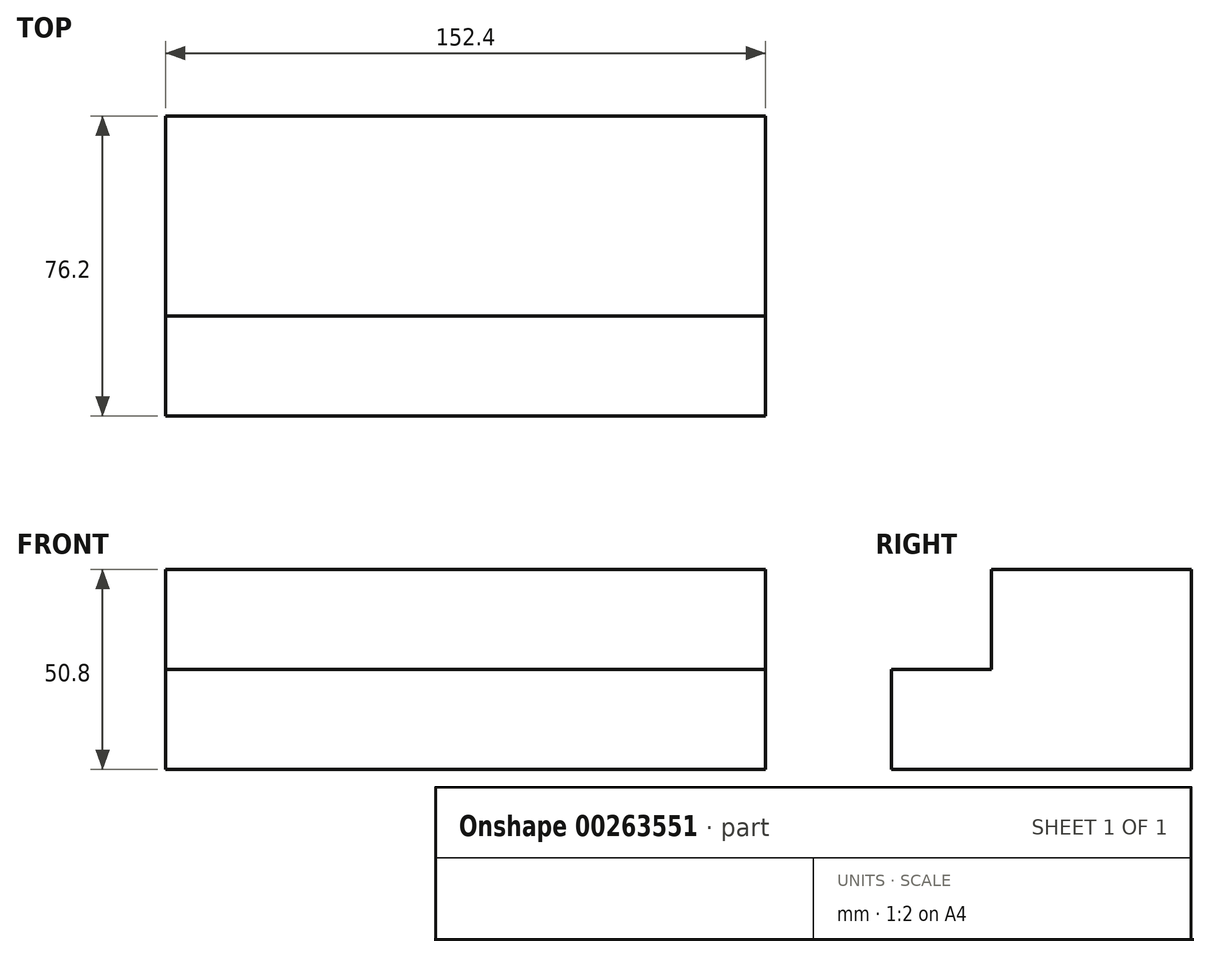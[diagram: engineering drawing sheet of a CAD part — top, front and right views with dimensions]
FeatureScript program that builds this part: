
annotation { "Feature Type Name" : "Feature", "Feature Type Description" : "" }
export const myFeature = defineFeature(function(context is Context, id is Id, definition is map)
    precondition{}
    {
        {
            var Q0;
            Q0=qCreatedBy(makeId("Front.planeOp"),FACE);
            var sketch = newSketch(context, id + "F0", { "sketchPlane" : qUnion([Q0])});
            skLineSegment(sketch, "E0", {"start": v(-61.88, -38.85) * mm, "end": v(90.52, -38.85) * mm});
            skLineSegment(sketch, "E1", {"start": v(-61.88, -38.85) * mm, "end": v(-61.88, -13.45) * mm});
            skLineSegment(sketch, "E2", {"start": v(-61.88, -13.45) * mm, "end": v(-61.88, 11.95) * mm});
            skLineSegment(sketch, "E3", {"start": v(90.52, -38.85) * mm, "end": v(90.52, -13.45) * mm});
            skLineSegment(sketch, "E4", {"start": v(90.52, -13.45) * mm, "end": v(90.52, 11.95) * mm});
            skLineSegment(sketch, "E5", {"start": v(90.52, 11.95) * mm, "end": v(-61.88, 11.95) * mm});
            skSolve(sketch);
        }
        {
            var Q0;
            Q0=makeQuery(id+"F0.imprint","IMPRINT",FACE,{"disambiguationData":[TD([[makeQuery(id+"F0.imprint","IMPRINT",EDGE,{"derivedFrom":sQuery(id+"F0.wireOp",EDGE,"E0")}),1.0]])]});
            extrude(context, id + "F1", {"entities" : qUnion([Q0]), "depth" : 76.2 * mm});
        }
        {
            var Q0;
            Q0=makeQuery(id+"F1.opExtrude","SWEPT_FACE",FACE,{"disambiguationData":[OSD([sQuery(id+"F0.wireOp",EDGE,"E3"),sQuery(id+"F0.wireOp",EDGE,"E4")])]});
            var sketch = newSketch(context, id + "F2", { "sketchPlane" : qUnion([Q0])});
            skLineSegment(sketch, "E6", {"start": v(-76.2, -38.85) * mm, "end": v(-76.2, -13.45) * mm});
            skLineSegment(sketch, "E7", {"start": v(-76.2, -13.45) * mm, "end": v(-50.8, -13.45) * mm});
            skLineSegment(sketch, "E8", {"start": v(-50.8, -13.45) * mm, "end": v(-50.8, 11.95) * mm});
            skSolve(sketch);
        }
        {
            var Q0;
            {var subQ0=sQuery(id+"F2.wireOp",EDGE,"E7");Q0=makeQuery(id+"F2.imprint","IMPRINT",FACE,{"disambiguationData":[TD([[makeQuery(id+"F2.imprint","IMPRINT",EDGE,{"derivedFrom":subQ0}),1.0]])]});}
            extrude(context, id + "F3", {"entities" : qUnion([Q0]), "operationType" : NewBodyOperationType.REMOVE, "oppositeDirection" : true, "depth" : 152.4 * mm});
        }
    });
